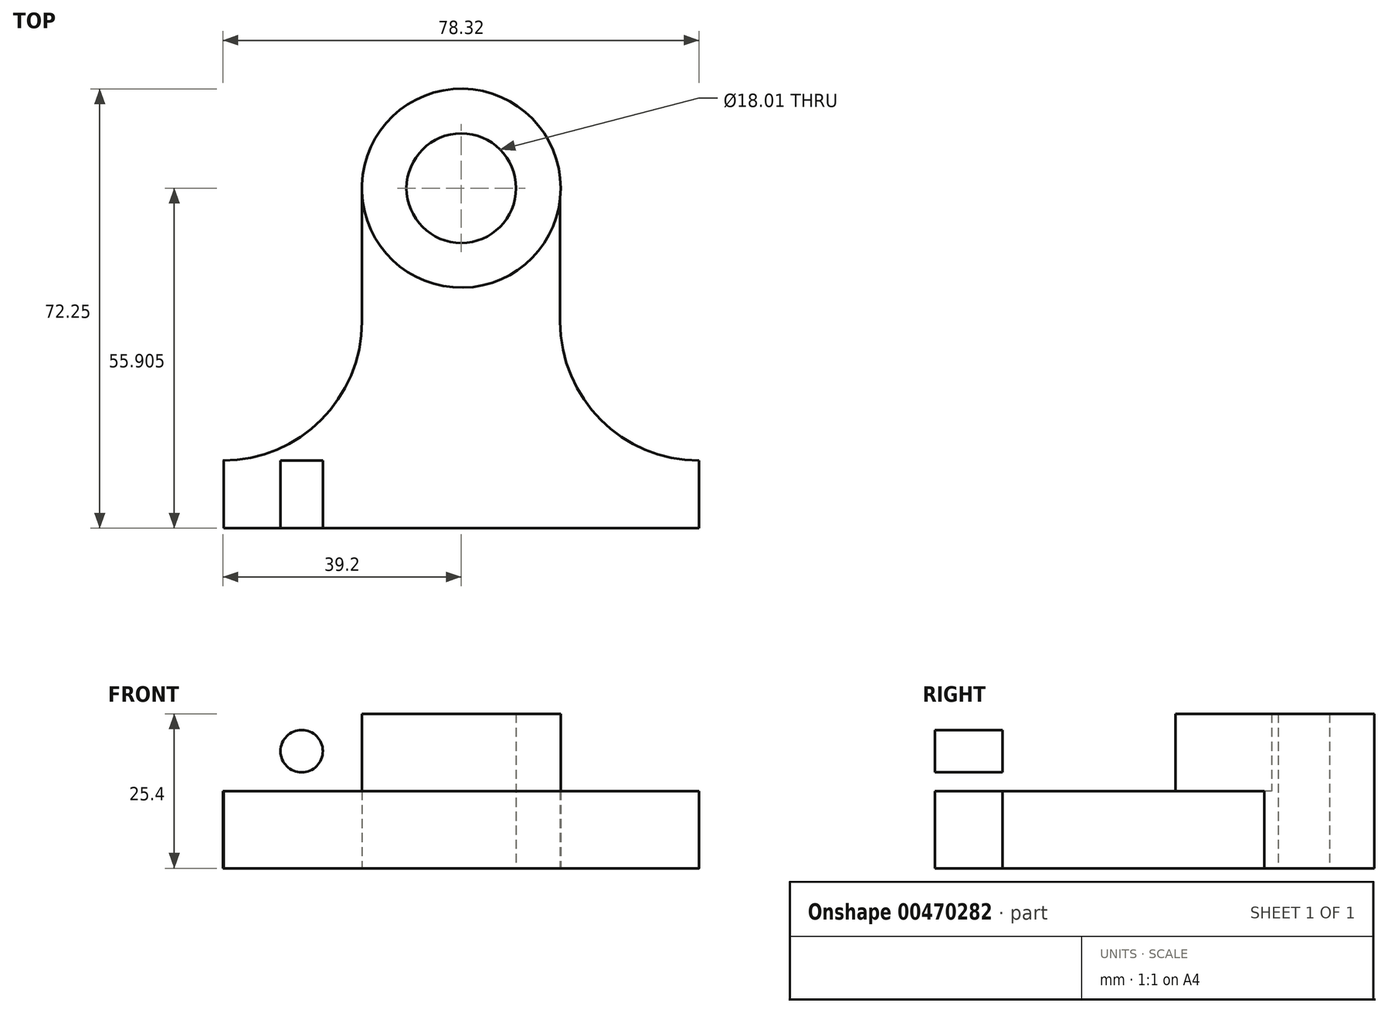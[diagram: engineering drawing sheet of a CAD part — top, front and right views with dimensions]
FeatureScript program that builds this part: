
annotation { "Feature Type Name" : "Feature", "Feature Type Description" : "" }
export const myFeature = defineFeature(function(context is Context, id is Id, definition is map)
    precondition{}
    {
        {
            var Q0;
            Q0=qCreatedBy(makeId("Top.planeOp"),FACE);
            var sketch = newSketch(context, id + "F0", { "sketchPlane" : qUnion([Q0])});
            skLineSegment(sketch, "E0.bottom", {"start": v(-39.2, 5.56) * mm, "end": v(-39.08, 5.56) * mm});
            skLineSegment(sketch, "E0.top", {"start": v(-39.08, -5.56) * mm, "end": v(39.08, -5.56) * mm});
            skLineSegment(sketch, "E0.left", {"start": v(-39.08, 5.56) * mm, "end": v(-39.08, -5.56) * mm});
            skLineSegment(sketch, "E0.right", {"start": v(39.08, 5.56) * mm, "end": v(39.08, -5.56) * mm});
            skPoint(sketch, "E0.middle", {"position": v(0, 0) * mm});
            skArc(sketch, "E1", {"start": v(16.26, 48.63) * mm, "mid": v(0.58, 66.68) * mm, "end": v(-16.34, 49.78) * mm});
            skLineSegment(sketch, "E2.left", {"start": v(-16.34, 50.9) * mm, "end": v(-16.34, 28.42) * mm});
            skLineSegment(sketch, "E2.right", {"start": v(16.26, 50.9) * mm, "end": v(16.26, 28.42) * mm});
            skLineSegment(sketch, "E3.trimOffspring", {"start": v(39.08, 5.56) * mm, "end": v(39.12, 5.56) * mm});
            skCircle(sketch, "E4", {"center": v(0, 50.34) * mm, "radius": 9 * mm});
            skPoint(sketch, "E5.visualSharp", {"position": v(16.26, 5.56) * mm});
            skArc(sketch, "E5.filletArc", {"start": v(16.26, 28.42) * mm, "mid": v(22.95, 12.26) * mm, "end": v(39.12, 5.56) * mm});
            skPoint(sketch, "E6.visualSharp", {"position": v(-16.34, 5.56) * mm});
            skArc(sketch, "E6.filletArc", {"start": v(-39.2, 5.56) * mm, "mid": v(-23.03, 12.26) * mm, "end": v(-16.34, 28.42) * mm});
            skLineSegment(sketch, "E7", {"start": v(-39.08, 5.56) * mm, "end": v(39.12, 5.56) * mm});
            skArc(sketch, "E8", {"start": v(-16.34, 49.78) * mm, "mid": v(-0.58, 34) * mm, "end": v(16.26, 48.63) * mm});
            skSolve(sketch);
        }
        {
            var Q0;
            Q0=makeQuery(id+"F0.imprint","IMPRINT",FACE,{"disambiguationData":[TD([[makeQuery(id+"F0.imprint","IMPRINT",EDGE,{"derivedFrom":sQuery(id+"F0.wireOp",EDGE,"E0.top")}),1.0]])]});
            var Q1;
            Q1=makeQuery(id+"F0.imprint","IMPRINT",FACE,{"disambiguationData":[TD([[makeQuery(id+"F0.imprint","IMPRINT",EDGE,{"derivedFrom":sQuery(id+"F0.wireOp",EDGE,"E4")}),-1.0]])]});
            extrude(context, id + "F1", {"entities" : qUnion([Q0, Q1]), "depth" : 25.4 * mm});
        }
        {
            var Q0;
            {var subQ6=sQuery(id+"F0.wireOp",EDGE,"E0.bottom");Q0=makeQuery(id+"F0.imprint","IMPRINT",FACE,{"disambiguationData":[TD([[makeQuery(id+"F0.imprint","IMPRINT",EDGE,{"derivedFrom":subQ6}),1.0]])]});}
            extrude(context, id + "F2", {"entities" : qUnion([Q0]), "operationType" : NewBodyOperationType.ADD, "depth" : 12.7 * mm});
        }
        {
            var Q0;
            Q0=makeQuery(id+"F1.opExtrude","CAP_EDGE",EDGE,{"disambiguationData":[OSD([sQuery(id+"F0.wireOp",EDGE,"E0.right")])],"isStart":false});
            var Q1;
            Q1=makeQuery(id+"F1.opExtrude","CAP_EDGE",EDGE,{"disambiguationData":[OSD([sQuery(id+"F0.wireOp",EDGE,"E0.left")])],"isStart":false});
            fillet(context, id + "F3", {"entities" : qUnion([Q0, Q1]), "radius" : 12.7 * mm, "tangentPropagation" : true, "allowEdgeOverflow" : false});
        }
        {
            var Q0;
            Q0=makeQuery(id+"F1.opExtrude","SWEPT_FACE",FACE,{"disambiguationData":[OSD([sQuery(id+"F0.wireOp",EDGE,"E7")])]});
            var sketch = newSketch(context, id + "F4", { "sketchPlane" : qUnion([Q0])});
            skCircle(sketch, "E9", {"center": v(-26.24, 19.25) * mm, "radius": 3.48 * mm});
            skCircle(sketch, "E10.MirrorC", {"center": v(26.24, 19.25) * mm, "radius": 3.48 * mm});
            skSolve(sketch);
        }
        {
            var Q0;
            Q0=makeQuery(id+"F4.imprint","IMPRINT",FACE,{"disambiguationData":[TD([[makeQuery(id+"F4.imprint","IMPRINT",EDGE,{"derivedFrom":sQuery(id+"F4.wireOp",EDGE,"E9")}),1.0]])]});
            var Q1;
            Q1=makeQuery(id+"F4.imprint","IMPRINT",FACE,{"disambiguationData":[TD([[makeQuery(id+"F4.imprint","IMPRINT",EDGE,{"derivedFrom":sQuery(id+"F4.wireOp",EDGE,"E10.MirrorC")}),-1.0]])]});
            extrude(context, id + "F5", {"entities" : qUnion([Q0, Q1]), "operationType" : NewBodyOperationType.REMOVE, "endBound" : BoundingType.THROUGH_ALL, "oppositeDirection" : true, "depth" : 25.4 * mm});
        }
    });
